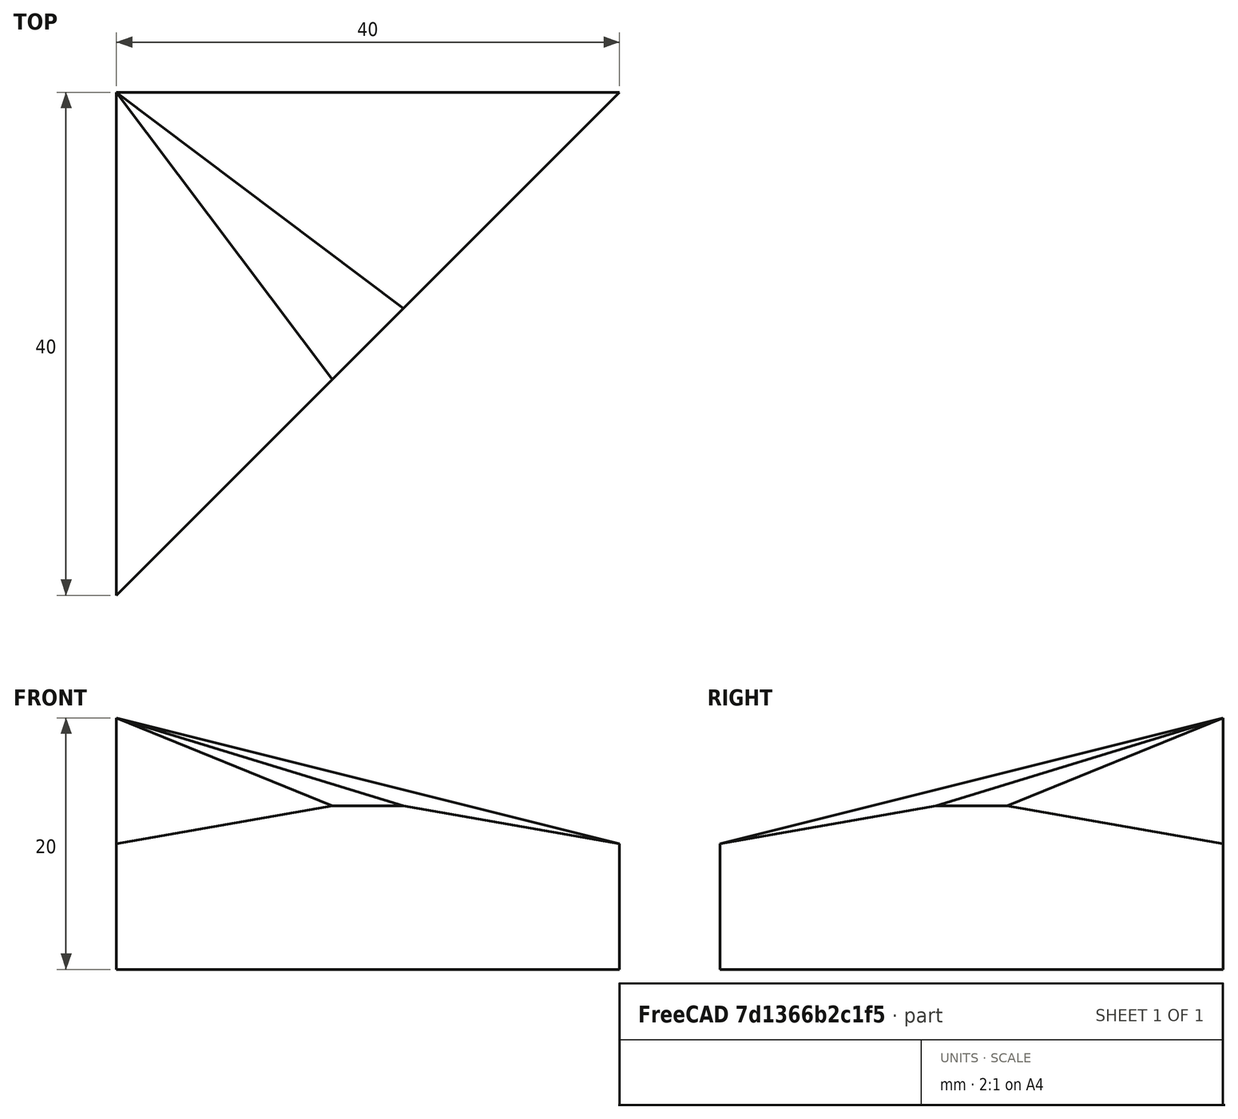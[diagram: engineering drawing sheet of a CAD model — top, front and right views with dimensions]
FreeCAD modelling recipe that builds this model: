
FCSTD DOCUMENT  (FreeCAD 0.21R33771 (Git))
Label: TEST001
License: All rights reserved
LicenseURL: http://en.wikipedia.org/wiki/All_rights_reserved
objects: Surface::Filling×7, Sketcher::SketchObject×5, PartDesign::Body×1, App::Part×1
note: 13 computed .brp shape members not serialized (recipe doc carries the construction recipe); baked Part::Feature solids carry a one-line shape summary decoded from their .brp

FEATURE [Sketcher::SketchObject] Sketch001
  FullyConstrained = true
  MapMode = 5
  Support = -> [XY_Plane001]
  sketch-geometry (4):
    g0: LineSegment StartX=-20 StartY=0 StartZ=0 EndX=-20 EndY=-40 EndZ=0
    g1: LineSegment StartX=-20 StartY=-40 StartZ=0 EndX=20 EndY=0 EndZ=0
    g2: LineSegment StartX=-20 StartY=0 StartZ=0 EndX=20 EndY=0 EndZ=0
    g3: GeomPoint X=20 Y=-1.68e-14 Z=0
  constraints (10):
    c: Vertical(g0)
    c: Coincident(g1,g0)
    c: Coincident(g2,g0)
    c: Coincident(g2,g1)
    c: Equal(g2,g0)
    c: PointOnObject(g3,g1)
    c: Symmetric(g3,g0,g-1)
    c: Horizontal(g2)
    c: DistanceX(g2,g2) = 40
    c: PointOnObject(g0,g-1)
FEATURE [Sketcher::SketchObject] Sketch
  ExternalGeometry = -> [Sketch001]
  FullyConstrained = true
  MapMode = 5
  Placement = pos=(0,0,0) rot=(1,0,0;1.5708rad)
  Support = -> [XZ_Plane001]
  sketch-geometry (4):
    g0: LineSegment StartX=-20 StartY=-7.1e-15 StartZ=0 EndX=20 EndY=0 EndZ=0
    g1: LineSegment StartX=20 StartY=0 StartZ=0 EndX=20 EndY=10 EndZ=0
    g2: LineSegment StartX=-20 StartY=20 StartZ=0 EndX=-20 EndY=-7.1e-15 EndZ=0
    g3: LineSegment StartX=20 StartY=10 StartZ=0 EndX=-20 EndY=20 EndZ=0
  constraints (10):
    c: Coincident(g0,g1)
    c: Coincident(g2,g0)
    c: Vertical(g1)
    c: Vertical(g2)
    c: Coincident(g0,g-4)
    c: Coincident(g0,g-4)
    c: Coincident(g3,g1)
    c: Coincident(g3,g2)
    c: DistanceY(g2,g2) = 20
    c: DistanceY(g1,g1) = 10
FEATURE [Sketcher::SketchObject] Sketch002
  ExternalGeometry = -> [Sketch,Sketch001]
  FullyConstrained = true
  MapMode = 13
  Placement = pos=(-20,-13.3333,6.66667) rot=(0.57735,-0.57735,-0.57735;2.0944rad)
  Support = -> [Sketch001,Sketch]
  sketch-geometry (4):
    g0: LineSegment StartX=-13.3333 StartY=13.3333 StartZ=0 EndX=26.6667 EndY=3.33333 EndZ=0
    g1: LineSegment StartX=26.6667 StartY=3.33333 StartZ=0 EndX=26.6667 EndY=-6.66667 EndZ=0
    g2: LineSegment StartX=26.6667 StartY=-6.66667 StartZ=0 EndX=-13.3333 EndY=-6.66667 EndZ=0
    g3: LineSegment StartX=-13.3333 StartY=-6.66667 StartZ=0 EndX=-13.3333 EndY=13.3333 EndZ=0
  constraints (10):
    c: Coincident(g0,g1)
    c: Coincident(g1,g2)
    c: Coincident(g2,g3)
    c: Coincident(g3,g0)
    c: Horizontal(g2)
    c: Vertical(g1)
    c: Vertical(g3)
    c: Coincident(g0,g-3)
    c: Coincident(g1,g-4)
    c: DistanceY(g1,g1) = 10
FEATURE [Sketcher::SketchObject] Sketch003
  ExternalGeometry = -> [Sketch001,Sketch002,Sketch]
  FullyConstrained = true
  MapMode = 13
  Placement = pos=(-6.66667,-26.6667,3.33333) rot=(0.862856,0.357407,0.357407;1.71777rad)
  Support = -> [Sketch001,Sketch002]
  sketch-geometry (7):
    g0: LineSegment StartX=13.4281 StartY=9.66667 StartZ=0 EndX=37.7124 EndY=6.66667 EndZ=0
    g1: LineSegment StartX=13.4281 StartY=9.66667 StartZ=0 EndX=5.42809 EndY=9.66667 EndZ=0
    g2: LineSegment StartX=5.42809 StartY=9.66667 StartZ=0 EndX=-18.8562 EndY=6.66667 EndZ=0
    g3: LineSegment StartX=-18.8562 StartY=6.66667 StartZ=0 EndX=-18.8562 EndY=-3.33333 EndZ=0
    g4: LineSegment StartX=-18.8562 StartY=-3.33333 StartZ=0 EndX=37.7124 EndY=-3.33333 EndZ=0
    g5: LineSegment StartX=37.7124 StartY=-3.33333 StartZ=0 EndX=37.7124 EndY=6.66667 EndZ=0
    g6: LineSegment StartX=9.42809 StartY=9.66667 StartZ=0 EndX=9.42809 EndY=-3.33333 EndZ=0
  constraints (16):
    c: Coincident(g0,g-5)
    c: Coincident(g0,g1)
    c: Horizontal(g1)
    c: Coincident(g1,g2)
    c: Coincident(g2,g-4)
    c: Coincident(g2,g3)
    c: Coincident(g3,g-4)
    c: Coincident(g3,g4)
    c: Coincident(g4,g-5)
    c: Coincident(g4,g5)
    c: Coincident(g5,g0)
    c: Coincident(g6,g-6)
    c: Vertical(g6)
    c: Symmetric(g1,g0,g6)
    c: DistanceY(g6,g6) = 13
    c: DistanceX(g1,g1) = 8
FEATURE [Sketcher::SketchObject] Sketch004
  ExternalGeometry = -> [Sketch003,Sketch002,Sketch]
  FullyConstrained = true
  MapMode = 13
  Placement = pos=(-6.66667,-13.3333,15.3333) rot=(-0.380279,0.918075,0.111918;3.23424rad)
  Support = -> [Sketch,Sketch003]
  sketch-geometry (3):
    g0: LineSegment StartX=4 StartY=-9.71253 StartZ=0 EndX=4e-16 EndY=19.4251 EndZ=0
    g1: LineSegment StartX=-4 StartY=-9.71253 StartZ=0 EndX=-4e-16 EndY=19.4251 EndZ=0
    g2: LineSegment StartX=4 StartY=-9.71253 StartZ=0 EndX=-4 EndY=-9.71253 EndZ=0
  constraints (6):
    c: Coincident(g-3,g0)
    c: Coincident(g0,g-5)
    c: Coincident(g-3,g1)
    c: Coincident(g1,g0)
    c: Coincident(g0,g2)
    c: Coincident(g2,g1)
FEATURE [PartDesign::Body] Body
  Group = -> [Sketch001,Sketch,Sketch002,Sketch003,Sketch004]
  Origin = -> Origin001
FEATURE [App::Part] Part
  Group = -> [Body]
  Origin = -> Origin
FEATURE [Surface::Filling] Surface
  Anisotropy = false
  BoundaryEdges = -> [Sketch001]
  BoundaryOrder = [0,0,0]
  Degree = 3
  Iterations = 2
  MaximumDegree = 8
  MaximumSegments = 9
  PointsOnCurve = 15
  TolAngular = 0.01
  TolCurvature = 0.1
  Tolerance2d = 1e-05
  Tolerance3d = 0.0001
FEATURE [Surface::Filling] Surface001
  Anisotropy = false
  BoundaryEdges = -> [Sketch,Sketch001]
  BoundaryOrder = [0,0,0,0]
  Degree = 3
  Iterations = 2
  MaximumDegree = 8
  MaximumSegments = 9
  PointsOnCurve = 15
  TolAngular = 0.01
  TolCurvature = 0.1
  Tolerance2d = 1e-05
  Tolerance3d = 0.0001
FEATURE [Surface::Filling] Surface002
  Anisotropy = false
  BoundaryEdges = -> [Sketch002,Sketch]
  BoundaryOrder = [0,0,0,0]
  Degree = 3
  Iterations = 2
  MaximumDegree = 8
  MaximumSegments = 9
  PointsOnCurve = 15
  TolAngular = 0.01
  TolCurvature = 0.1
  Tolerance2d = 1e-05
  Tolerance3d = 0.0001
FEATURE [Surface::Filling] Surface003
  Anisotropy = false
  BoundaryEdges = -> [Sketch003,Surface001,Surface]
  BoundaryOrder = [0,0,0,0,0,0]
  Degree = 3
  Iterations = 2
  MaximumDegree = 8
  MaximumSegments = 9
  PointsOnCurve = 15
  TolAngular = 0.01
  TolCurvature = 0.1
  Tolerance2d = 1e-05
  Tolerance3d = 0.0001
FEATURE [Surface::Filling] Surface004
  Anisotropy = false
  BoundaryEdges = -> [Surface002,Sketch004,Surface003]
  BoundaryOrder = [0,0,0]
  Degree = 3
  Iterations = 2
  MaximumDegree = 8
  MaximumSegments = 9
  PointsOnCurve = 15
  TolAngular = 0.01
  TolCurvature = 0.1
  Tolerance2d = 1e-05
  Tolerance3d = 0.0001
FEATURE [Surface::Filling] Surface005
  Anisotropy = false
  BoundaryEdges = -> [Surface004,Sketch004]
  BoundaryOrder = [0,0,0]
  Degree = 3
  Iterations = 2
  MaximumDegree = 8
  MaximumSegments = 9
  PointsOnCurve = 15
  TolAngular = 0.01
  TolCurvature = 0.1
  Tolerance2d = 1e-05
  Tolerance3d = 0.0001
FEATURE [Surface::Filling] Surface006
  Anisotropy = false
  BoundaryEdges = -> [Surface001,Surface003,Surface005]
  BoundaryOrder = [0,0,0]
  Degree = 3
  Iterations = 2
  MaximumDegree = 8
  MaximumSegments = 9
  PointsOnCurve = 15
  TolAngular = 0.01
  TolCurvature = 0.1
  Tolerance2d = 1e-05
  Tolerance3d = 0.0001
